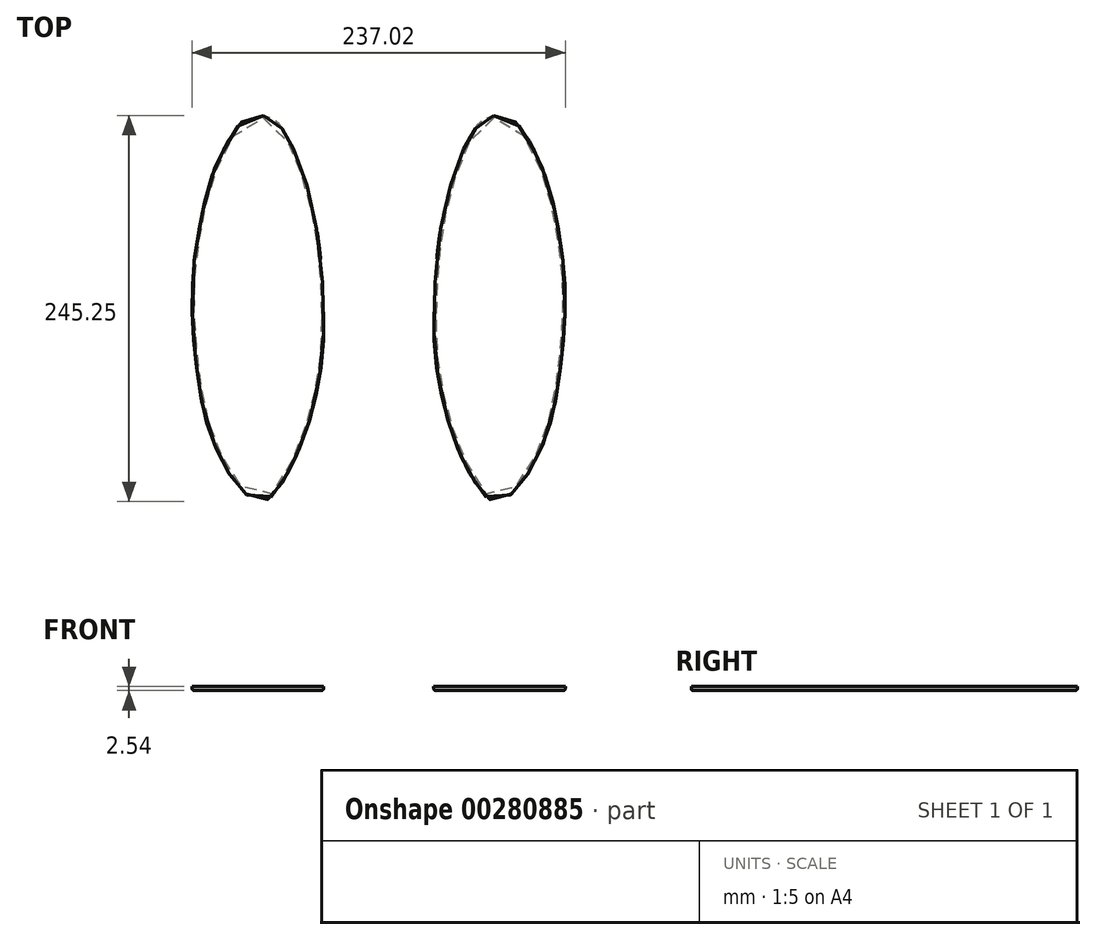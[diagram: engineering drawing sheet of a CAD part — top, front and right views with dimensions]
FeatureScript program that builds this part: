
annotation { "Feature Type Name" : "Feature", "Feature Type Description" : "" }
export const myFeature = defineFeature(function(context is Context, id is Id, definition is map)
    precondition{}
    {
        {
            var Q0;
            Q0=qCreatedBy(makeId("Top.planeOp"),FACE);
            var sketch = newSketch(context, id + "F0", { "sketchPlane" : qUnion([Q0])});
            skPoint(sketch, "E0", {"position": v(0, 122.5) * mm});
            skLineSegment(sketch, "E1", {"start": v(0, 122.5) * mm, "end": v(0, 120) * mm, "construction": true});
            skLineSegment(sketch, "E2", {"start": v(0, 120) * mm, "end": v(0, 117.5) * mm, "construction": true});
            skLineSegment(sketch, "E3", {"start": v(0, 117.5) * mm, "end": v(0, 112.5) * mm, "construction": true});
            skLineSegment(sketch, "E4", {"start": v(0, 112.5) * mm, "end": v(0, 107.5) * mm, "construction": true});
            skLineSegment(sketch, "E5", {"start": v(0, 107.5) * mm, "end": v(0, 102.5) * mm, "construction": true});
            skLineSegment(sketch, "E6", {"start": v(0, 102.5) * mm, "end": v(0, 92.5) * mm, "construction": true});
            skLineSegment(sketch, "E7", {"start": v(0, 92.5) * mm, "end": v(0, 72.5) * mm, "construction": true});
            skLineSegment(sketch, "E8", {"start": v(0, 72.5) * mm, "end": v(0, 52.5) * mm, "construction": true});
            skLineSegment(sketch, "E9", {"start": v(0, 52.5) * mm, "end": v(0, 22.5) * mm, "construction": true});
            skLineSegment(sketch, "E10", {"start": v(0, 22.5) * mm, "end": v(0, -7.5) * mm, "construction": true});
            skLineSegment(sketch, "E11", {"start": v(0, -7.5) * mm, "end": v(0, -27.5) * mm, "construction": true});
            skLineSegment(sketch, "E12", {"start": v(0, -27.5) * mm, "end": v(0, -47.5) * mm, "construction": true});
            skLineSegment(sketch, "E13", {"start": v(0, -47.5) * mm, "end": v(0, -67.5) * mm, "construction": true});
            skLineSegment(sketch, "E14", {"start": v(0, -67.5) * mm, "end": v(0, -87.5) * mm, "construction": true});
            skLineSegment(sketch, "E15", {"start": v(0, -87.5) * mm, "end": v(0, -97.5) * mm, "construction": true});
            skLineSegment(sketch, "E16", {"start": v(0, -97.5) * mm, "end": v(0, -107.5) * mm, "construction": true});
            skLineSegment(sketch, "E17", {"start": v(0, -107.5) * mm, "end": v(0, -112.5) * mm, "construction": true});
            skLineSegment(sketch, "E18", {"start": v(0, -112.5) * mm, "end": v(0, -117.5) * mm, "construction": true});
            skLineSegment(sketch, "E19", {"start": v(0, -117.5) * mm, "end": v(0, -120) * mm, "construction": true});
            skLineSegment(sketch, "E20", {"start": v(0, -120) * mm, "end": v(0, -122.5) * mm, "construction": true});
            skLineSegment(sketch, "E21", {"start": v(0, -7.5) * mm, "end": v(40, -7.5) * mm, "construction": true});
            skLineSegment(sketch, "E22", {"start": v(0, -7.5) * mm, "end": v(-43.2, -7.5) * mm, "construction": true});
            skLineSegment(sketch, "E23", {"start": v(0, 120) * mm, "end": v(8.2, 120) * mm, "construction": true});
            skLineSegment(sketch, "E24", {"start": v(0, 117.5) * mm, "end": v(11.3, 117.5) * mm, "construction": true});
            skLineSegment(sketch, "E25", {"start": v(0, 112.5) * mm, "end": v(15, 112.5) * mm, "construction": true});
            skLineSegment(sketch, "E26", {"start": v(0, 107.5) * mm, "end": v(18.1, 107.5) * mm, "construction": true});
            skLineSegment(sketch, "E27", {"start": v(0, 102.5) * mm, "end": v(20.5, 102.5) * mm, "construction": true});
            skLineSegment(sketch, "E28", {"start": v(0, 92.5) * mm, "end": v(24.7, 92.5) * mm, "construction": true});
            skLineSegment(sketch, "E29", {"start": v(0, 72.5) * mm, "end": v(31.1, 72.5) * mm, "construction": true});
            skLineSegment(sketch, "E30", {"start": v(0, 52.5) * mm, "end": v(35.4, 52.5) * mm, "construction": true});
            skLineSegment(sketch, "E31", {"start": v(0, 22.5) * mm, "end": v(38.9, 22.5) * mm, "construction": true});
            skLineSegment(sketch, "E32", {"start": v(0, 120) * mm, "end": v(-9.8, 120) * mm, "construction": true});
            skLineSegment(sketch, "E33", {"start": v(0, 117.5) * mm, "end": v(-12.9, 117.5) * mm, "construction": true});
            skLineSegment(sketch, "E34", {"start": v(0, 112.5) * mm, "end": v(-16.8, 112.5) * mm, "construction": true});
            skLineSegment(sketch, "E35", {"start": v(0, 107.5) * mm, "end": v(-20.2, 107.5) * mm, "construction": true});
            skLineSegment(sketch, "E36", {"start": v(0, 102.5) * mm, "end": v(-22.8, 102.5) * mm, "construction": true});
            skLineSegment(sketch, "E37", {"start": v(0, 92.5) * mm, "end": v(-27.7, 92.5) * mm, "construction": true});
            skLineSegment(sketch, "E38", {"start": v(0, 72.5) * mm, "end": v(-34.5, 72.5) * mm, "construction": true});
            skLineSegment(sketch, "E39", {"start": v(0, 52.5) * mm, "end": v(-38.7, 52.5) * mm, "construction": true});
            skLineSegment(sketch, "E40", {"start": v(0, 22.5) * mm, "end": v(-42.9, 22.5) * mm, "construction": true});
            skLineSegment(sketch, "E41", {"start": v(0, -27.5) * mm, "end": v(-41.7, -27.5) * mm, "construction": true});
            skLineSegment(sketch, "E42", {"start": v(0, -47.5) * mm, "end": v(-39.2, -47.5) * mm, "construction": true});
            skLineSegment(sketch, "E43", {"start": v(0, -67.5) * mm, "end": v(-35.5, -67.5) * mm, "construction": true});
            skLineSegment(sketch, "E44", {"start": v(0, -87.5) * mm, "end": v(-28.8, -87.5) * mm, "construction": true});
            skLineSegment(sketch, "E45", {"start": v(0, -97.5) * mm, "end": v(-24.1, -97.5) * mm, "construction": true});
            skLineSegment(sketch, "E46", {"start": v(0, -107.5) * mm, "end": v(-18.1, -107.5) * mm, "construction": true});
            skLineSegment(sketch, "E47", {"start": v(0, -112.5) * mm, "end": v(-14.4, -112.5) * mm, "construction": true});
            skLineSegment(sketch, "E48", {"start": v(0, -27.5) * mm, "end": v(39.4, -27.5) * mm, "construction": true});
            skLineSegment(sketch, "E49", {"start": v(0, -47.5) * mm, "end": v(36.6, -47.5) * mm, "construction": true});
            skLineSegment(sketch, "E50", {"start": v(0, -67.5) * mm, "end": v(32.1, -67.5) * mm, "construction": true});
            skLineSegment(sketch, "E51", {"start": v(0, -87.5) * mm, "end": v(25.3, -87.5) * mm, "construction": true});
            skLineSegment(sketch, "E52", {"start": v(0, -97.5) * mm, "end": v(21, -97.5) * mm, "construction": true});
            skLineSegment(sketch, "E53", {"start": v(0, -107.5) * mm, "end": v(15.5, -107.5) * mm, "construction": true});
            skLineSegment(sketch, "E54", {"start": v(0, -112.5) * mm, "end": v(12.5, -112.5) * mm, "construction": true});
            skLineSegment(sketch, "E55", {"start": v(0, -117.5) * mm, "end": v(8.8, -117.5) * mm, "construction": true});
            skLineSegment(sketch, "E56", {"start": v(0, -120) * mm, "end": v(6.3, -120) * mm, "construction": true});
            skLineSegment(sketch, "E57", {"start": v(0, -117.5) * mm, "end": v(-9.6, -117.5) * mm, "construction": true});
            skLineSegment(sketch, "E58", {"start": v(0, -120) * mm, "end": v(-6.4, -120) * mm, "construction": true});
            skLineSegment(sketch, "E59", {"start": v(0, 122.5) * mm, "end": v(2, 122.5) * mm});
            skLineSegment(sketch, "E60", {"start": v(0, 122.5) * mm, "end": v(-2, 122.5) * mm, "construction": true});
            skFitSpline(sketch, "E61", {"points": [v(40, -7.5) * mm, v(38.9, 22.5) * mm, v(35.4, 52.5) * mm, v(31.1, 72.5) * mm, v(24.7, 92.5) * mm, v(20.5, 102.5) * mm, v(18.1, 107.5) * mm, v(15, 112.5) * mm, v(11.3, 117.5) * mm, v(8.2, 120) * mm, v(2, 122.5) * mm, v(-2, 122.5) * mm, v(-9.8, 120) * mm, v(-12.9, 117.5) * mm, v(-16.8, 112.5) * mm, v(-20.2, 107.5) * mm, v(-22.8, 102.5) * mm, v(-27.7, 92.5) * mm, v(-34.5, 72.5) * mm, v(-38.7, 52.5) * mm, v(-42.9, 22.5) * mm, v(-43.2, -7.5) * mm, v(-41.7, -27.5) * mm, v(-39.2, -47.5) * mm, v(-35.5, -67.5) * mm, v(-28.8, -87.5) * mm, v(-24.1, -97.5) * mm, v(-18.1, -107.5) * mm, v(-14.4, -112.5) * mm, v(-9.6, -117.5) * mm, v(-6.4, -120) * mm, v(0, -122.5) * mm, v(6.3, -120) * mm, v(8.8, -117.5) * mm, v(12.5, -112.5) * mm, v(15.5, -107.5) * mm, v(21, -97.5) * mm, v(25.3, -87.5) * mm, v(32.1, -67.5) * mm, v(36.6, -47.5) * mm, v(39.4, -27.5) * mm, v(40, -7.5) * mm]});
            skSolve(sketch);
        }
        {
            var Q0;
            Q0=qSketchRegion(id+"F0",true);
            extrude(context, id + "F1", {"entities" : qUnion([Q0]), "depth" : 2.54 * mm});
        }
        {
            var Q0;
            Q0=makeQuery(id+"F1.opExtrude","CAP_EDGE",EDGE,{"disambiguationData":[OSD([sQuery(id+"F0.wireOp",EDGE,"E61")])],"isStart":true});
            fillet(context, id + "F2", {"entities" : qUnion([Q0]), "radius" : 1.27 * mm, "tangentPropagation" : true, "allowEdgeOverflow" : false});
        }
        {
            var Q0;
            Q0=qCreatedBy(makeId("Right.planeOp"),FACE);
            cPlane(context, id + "F3", {"entities" : qUnion([Q0]), "cplaneType" : CPlaneType.OFFSET, "offset" : 75 * mm, "width" : 150 * mm, "height" : 150 * mm});
        }
        {
            var Q0;
            Q0=makeQuery(id+"F1.opExtrude","SWEPT_BODY",BODY,{"disambiguationData":[OSD([sQuery(id+"F0.wireOp",EDGE,"E61")])]});
            var Q1;
            Q1=qCreatedBy(id+"F3.planeOp",FACE);
            mirror(context, id + "F4", {"entities" : qUnion([Q0]), "mirrorPlane" : qUnion([Q1])});
        }
    });
